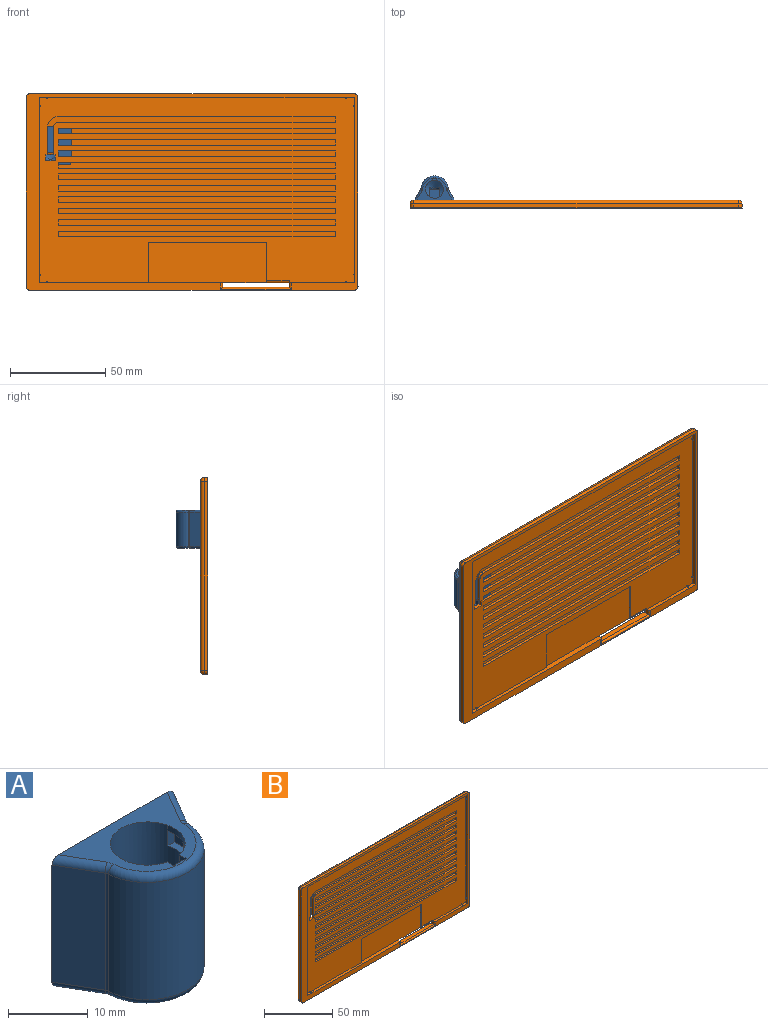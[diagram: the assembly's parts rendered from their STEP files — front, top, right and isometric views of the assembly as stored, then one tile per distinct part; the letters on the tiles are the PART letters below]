
ASSEMBLY  parts=2 mates=1
PART A: 43 faces, bbox 23.9x16.6x22.3 mm
  f0: plane 8.9x4.8mm, normal (0,0,1), area 1.2mm2, adj f21,f32,f34,f40
  f1: cylinder r=4.7mm len=15mm, axis (0,0,1), area 384mm2, adj f2,f7,f21,f23,f25,f31,f32,f33
  f2: cylinder r=4.7mm len=5.57mm, axis (0,0,1), area 6.6mm2, adj f1,f7,f24,f27
  f3: plane 18x5.99mm, normal (-0.86,-0.5,0), area 124.6mm2, adj f6,f11,f17,f20
  f4: cylinder r=7.2mm len=18mm, axis (0,0,-1), area 391.8mm2, adj f12,f13,f17,f18
  f5: plane 18x5.99mm, normal (0.86,-0.5,0), area 124.6mm2, adj f6,f9,f13,f14
  f6: plane 21.84x20.24mm, normal (0,1,0), area 406mm2, adj f3,f5,f7,f8,f9,f11,f14,f20
  f7: plane 19.29x12.2mm, normal (0,0,1), area 83.6mm2, adj f1,f2,f6,f9,f10,f11,f12,f15
  f8: plane 19.29x12.2mm, normal (0,0,-1), area 155.3mm2, adj f6,f14,f16,f18,f19,f20
  f9: cylinder r=1mm len=6.49mm, axis (-0.5,-0.86,0), area 10.4mm2, adj f5,f6,f7,f10
  f10: torus R=2mm, axis (0,0,1), area 1mm2, adj f7,f9,f12,f13
  f11: cylinder r=1mm len=6.49mm, axis (-0.5,0.86,0), area 10.4mm2, adj f3,f6,f7,f15
  f12: torus R=6.2mm, axis (0,0,1), area 32.5mm2, adj f4,f7,f10,f15
  f13: cylinder r=1mm len=18mm, axis (0,0,-1), area 8.4mm2, adj f4,f5,f10,f16
  f14: cylinder r=1mm len=6.49mm, axis (0.5,0.86,0), area 10.4mm2, adj f5,f6,f8,f16
  f15: torus R=2mm, axis (0,0,1), area 1mm2, adj f7,f11,f12,f17
  f16: torus R=2mm, axis (0,0,1), area 1mm2, adj f8,f13,f14,f18
  f17: cylinder r=1mm len=18mm, axis (0,0,-1), area 8.4mm2, adj f3,f4,f15,f19
  f18: torus R=6.2mm, axis (0,0,1), area 32.5mm2, adj f4,f8,f16,f19
  f19: torus R=2mm, axis (0,0,1), area 1mm2, adj f8,f17,f18,f20
  f20: cylinder r=1mm len=6.49mm, axis (0.5,-0.86,0), area 10.4mm2, adj f3,f6,f8,f19
  f21: cone r=0mm half-angle=57.4deg, axis (0,0,1), area 41.7mm2, adj f0,f1,f39,f40,f41
  f22: plane 3.1x2.2mm, normal (0,1,0), area 6.8mm2, adj f7,f23,f24,f25,f28
  f23: plane 6.8x6.7mm, normal (0,0,1), area 9.2mm2, adj f1,f22,f25,f26,f28,f29,f30,f31
  f24: plane 1.13x0.9mm, normal (-1,0,0), area 1mm2, adj f2,f7,f22,f27
  f25: plane 3.1x1.13mm, normal (1,0,0), area 3.5mm2, adj f1,f7,f22,f23
  f26: cylinder r=5.5mm len=4.04mm, axis (0,0,-1), area 11.8mm2, adj f23,f27,f28,f30
  f27: plane 6.7x4.6mm, normal (0,0,-1), area 6.9mm2, adj f2,f24,f26,f28,f29,f30,f31
  f28: cylinder r=5mm len=2.2mm, axis (0,0,1), area 2.8mm2, adj f22,f23,f26,f27
  f29: plane 2.2x2mm, normal (-1,0,0), area 4.4mm2, adj f23,f27,f30,f31
  f30: plane 2.2x0.29mm, normal (0,1,0), area 0.6mm2, adj f23,f26,f27,f29
  f31: plane 2.2x1.11mm, normal (0,-1,0), area 2.4mm2, adj f1,f23,f27,f29
  f32: plane 2x0.1mm, normal (-1,0,0), area 0.2mm2, adj f0,f1,f33,f34
  f33: plane 9.6x4.8mm, normal (0,0,-1), area 1.5mm2, adj f1,f32,f34,f35
  f34: cylinder r=4.8mm len=9.6mm, axis (0,0,-1), area 30.2mm2, adj f0,f32,f33,f35,f37
  f35: plane 2x0.1mm, normal (-1,0,0), area 0.2mm2, adj f1,f33,f34,f37
  f36: plane 6.2x5mm, normal (0,0,1), area 31mm2, adj f6,f38,f39,f40
  f37: plane 5x1.22mm, normal (0,0,-1), area 3.4mm2, adj f1,f34,f35,f39,f40,f42
  f38: plane 5x1.53mm, normal (0,1,0), area 4.4mm2, adj f36,f39,f40,f41
  f39: plane 9.29x7.26mm, normal (-1,0,0), area 21.7mm2, adj f6,f21,f36,f37,f38,f41,f42
  f40: plane 9.29x7.26mm, normal (1,0,0), area 21.7mm2, adj f0,f6,f21,f36,f37,f38,f41,f42
  f41: bspline ~7.09x2.62mm, area 6.9mm2, adj f21,f38,f39,f40
  f42: cylinder r=1mm len=5mm, axis (-1,0,0), area 7.9mm2, adj f6,f37,f39,f40
PART B: 133 faces, bbox 174x4x103 mm
  f0: plane 2x0.94mm, normal (0,0,-1), area 1.9mm2, adj f2,f38,f40,f57
  f1: plane 62x21mm, normal (0,-1,0), area 1302mm2, adj f3,f4,f5,f102,f127
  f2: plane 170x99mm, normal (0,1,0), area 16703.9mm2, adj f0,f38,f39,f40,f41,f42,f43,f119
  f3: plane 21x1mm, normal (-1,0,0), area 20.8mm2, adj f1,f4,f57,f127
  f4: plane 62x1mm, normal (0,0,-1), area 62mm2, adj f1,f3,f5,f57
  f5: plane 21x1mm, normal (1,0,0), area 21mm2, adj f1,f4,f57,f102
  f6: plane 3x1.5mm, normal (1,0,0), area 4.5mm2, adj f7,f56,f57,f59
  f7: plane 145x1.5mm, normal (0,0,-1), area 217.5mm2, adj f6,f8,f57,f59
  f8: plane 3x1.5mm, normal (-1,0,0), area 4.5mm2, adj f7,f56,f57,f59
  f9: plane 3x1.5mm, normal (1,0,0), area 4.5mm2, adj f10,f46,f57,f60
  f10: plane 145x1.5mm, normal (0,0,-1), area 217.5mm2, adj f9,f11,f57,f60
  f11: plane 3x1.5mm, normal (-1,0,0), area 4.5mm2, adj f10,f46,f57,f60
  f12: plane 3x1.5mm, normal (1,0,0), area 4.5mm2, adj f13,f47,f57,f61
  f13: plane 145x1.5mm, normal (0,0,-1), area 217.5mm2, adj f12,f14,f57,f61
  f14: plane 3x1.5mm, normal (-1,0,0), area 4.5mm2, adj f13,f47,f57,f61
  f15: plane 3x1.5mm, normal (1,0,0), area 4.5mm2, adj f16,f48,f57,f62
  f16: plane 145x1.5mm, normal (0,0,-1), area 217.5mm2, adj f15,f17,f57,f62
  f17: plane 3x1.5mm, normal (-1,0,0), area 4.5mm2, adj f16,f48,f57,f62
  f18: plane 3x1.5mm, normal (1,0,0), area 4.5mm2, adj f19,f49,f57,f63
  f19: plane 145x1.5mm, normal (0,0,-1), area 217.5mm2, adj f18,f20,f57,f63
  f20: plane 3x1.5mm, normal (-1,0,0), area 4.5mm2, adj f19,f49,f57,f63
  f21: plane 3x1.5mm, normal (1,0,0), area 4.5mm2, adj f22,f50,f57,f64
  f22: plane 145x1.5mm, normal (0,0,-1), area 217.5mm2, adj f21,f23,f57,f64
  f23: plane 3x1.5mm, normal (-1,0,0), area 4.5mm2, adj f22,f50,f57,f64
  f24: plane 3x1.5mm, normal (1,0,0), area 4.5mm2, adj f25,f51,f57,f65
  f25: plane 145x1.5mm, normal (0,0,-1), area 217.5mm2, adj f24,f26,f57,f65
  f26: plane 3x1.5mm, normal (-1,0,0), area 4.5mm2, adj f25,f51,f57,f65
  f27: plane 3x1.5mm, normal (1,0,0), area 4.5mm2, adj f28,f52,f57,f66
  f28: plane 145x1.5mm, normal (0,0,-1), area 217.5mm2, adj f27,f29,f57,f66
  f29: plane 3x1.5mm, normal (-1,0,0), area 4.5mm2, adj f28,f52,f57,f66
  f30: plane 3x1.5mm, normal (1,0,0), area 4.5mm2, adj f31,f53,f57,f67
  f31: plane 145x1.5mm, normal (0,0,-1), area 217.5mm2, adj f30,f32,f57,f67
  f32: plane 3x1.5mm, normal (-1,0,0), area 4.5mm2, adj f31,f53,f57,f67
  f33: plane 3x1.5mm, normal (1,0,0), area 4.5mm2, adj f34,f54,f57,f68
  f34: plane 145x1.5mm, normal (0,0,-1), area 217.5mm2, adj f33,f35,f57,f68
  f35: plane 3x1.5mm, normal (-1,0,0), area 4.5mm2, adj f34,f54,f57,f68
  f36: plane 145x1.5mm, normal (0,0,1), area 217.5mm2, adj f37,f55,f57,f58
  f37: cylinder r=2.64mm len=2.64mm, axis (0,1,0), area 6.2mm2, adj f36,f38,f57,f58
  f38: plane 14.36x2mm, normal (-1,0,0), area 21.7mm2, adj f0,f2,f37,f57,f58,f132
  f39: plane 2x0.96mm, normal (0,0,-1), area 1.9mm2, adj f2,f42,f43,f57
  f40: plane 3x2mm, normal (-1,0,0), area 6mm2, adj f0,f2,f41,f57
  f41: plane 4.9x2mm, normal (0,0,1), area 9.8mm2, adj f2,f40,f42,f57
  f42: plane 3x2mm, normal (1,0,0), area 6mm2, adj f2,f39,f41,f57
  f43: plane 14.36x2mm, normal (1,0,0), area 21.7mm2, adj f2,f39,f44,f57,f58,f132
  f44: cylinder r=5.64mm len=5.64mm, axis (0,1,0), area 13.3mm2, adj f43,f45,f57,f58
  f45: plane 145x1.5mm, normal (0,0,-1), area 217.5mm2, adj f44,f55,f57,f58
  f46: plane 145x1.5mm, normal (0,0,1), area 217.5mm2, adj f9,f11,f57,f60
  f47: plane 145x1.5mm, normal (0,0,1), area 217.5mm2, adj f12,f14,f57,f61
  f48: plane 145x1.5mm, normal (0,0,1), area 217.5mm2, adj f15,f17,f57,f62
  f49: plane 145x1.5mm, normal (0,0,1), area 217.5mm2, adj f18,f20,f57,f63
  f50: plane 145x1.5mm, normal (0,0,1), area 217.5mm2, adj f21,f23,f57,f64
  f51: plane 145x1.5mm, normal (0,0,1), area 217.5mm2, adj f24,f26,f57,f65
  f52: plane 145x1.5mm, normal (0,0,1), area 217.5mm2, adj f27,f29,f57,f66
  f53: plane 145x1.5mm, normal (0,0,1), area 217.5mm2, adj f30,f32,f57,f67
  f54: plane 145x1.5mm, normal (0,0,1), area 217.5mm2, adj f33,f35,f57,f68
  f55: plane 3x1.5mm, normal (-1,0,0), area 4.5mm2, adj f36,f45,f57,f58
  f56: plane 145x1.5mm, normal (0,0,1), area 217.5mm2, adj f6,f8,f57,f59
  f57: plane 165x97mm, normal (0,-1,0), area 9826.7mm2, adj f0,f3,f4,f5,f6,f7,f8,f9
  f58: plane 150.64x19mm, normal (0,-1,0), area 494.6mm2, adj f36,f37,f38,f43,f44,f45,f55,f132
  f59: plane 145x3mm, normal (0,-1,0), area 435mm2, adj f6,f7,f8,f56
  f60: plane 145x3mm, normal (0,-1,0), area 435mm2, adj f9,f10,f11,f46
  f61: plane 145x3mm, normal (0,-1,0), area 435mm2, adj f12,f13,f14,f47
  f62: plane 145x3mm, normal (0,-1,0), area 435mm2, adj f15,f16,f17,f48
  f63: plane 145x3mm, normal (0,-1,0), area 435mm2, adj f18,f19,f20,f49
  f64: plane 145x3mm, normal (0,-1,0), area 435mm2, adj f21,f22,f23,f50
  f65: plane 145x3mm, normal (0,-1,0), area 435mm2, adj f24,f25,f26,f51
  f66: plane 145x3mm, normal (0,-1,0), area 435mm2, adj f27,f28,f29,f52
  f67: plane 145x3mm, normal (0,-1,0), area 435mm2, adj f30,f31,f32,f53
  f68: plane 145x3mm, normal (0,-1,0), area 435mm2, adj f33,f34,f35,f54
  f69: plane 1x0.5mm, normal (1,0,0), area 0.5mm2, adj f57,f70,f72,f101
  f70: plane 1x0.5mm, normal (0,0,-1), area 0.5mm2, adj f57,f69,f71,f72
  f71: plane 1x0.5mm, normal (-1,0,0), area 0.5mm2, adj f57,f70,f72,f101
  f72: plane 0.5x0.5mm, normal (0,-1,0), area 0.3mm2, adj f69,f70,f71,f101
  f73: plane 1x0.5mm, normal (1,0,0), area 0.5mm2, adj f57,f74,f76,f101
  f74: plane 1x0.5mm, normal (0,0,-1), area 0.5mm2, adj f57,f73,f75,f76
  f75: plane 1x0.5mm, normal (-1,0,0), area 0.5mm2, adj f57,f74,f76,f101
  f76: plane 0.5x0.5mm, normal (0,-1,0), area 0.3mm2, adj f73,f74,f75,f101
  f77: plane 1x0.5mm, normal (-1,0,0), area 0.5mm2, adj f57,f78,f80,f102
  f78: plane 1x0.5mm, normal (0,0,1), area 0.5mm2, adj f57,f77,f79,f80
  f79: plane 1x0.5mm, normal (1,0,0), area 0.5mm2, adj f57,f78,f80,f102
  f80: plane 0.5x0.5mm, normal (0,-1,0), area 0.3mm2, adj f77,f78,f79,f102
  f81: plane 1x0.5mm, normal (0,0,1), area 0.5mm2, adj f57,f82,f84,f103
  f82: plane 1x0.5mm, normal (1,0,0), area 0.5mm2, adj f57,f81,f83,f84
  f83: plane 1x0.5mm, normal (0,0,-1), area 0.5mm2, adj f57,f82,f84,f103
  f84: plane 0.5x0.5mm, normal (0,-1,0), area 0.3mm2, adj f81,f82,f83,f103
  f85: plane 1x0.5mm, normal (1,0,0), area 0.5mm2, adj f57,f86,f87,f88
  f86: plane 1x0.5mm, normal (0,0,-1), area 0.5mm2, adj f57,f85,f88,f103
  f87: plane 1x0.5mm, normal (0,0,1), area 0.5mm2, adj f57,f85,f88,f103
  f88: plane 0.5x0.5mm, normal (0,-1,0), area 0.3mm2, adj f85,f86,f87,f103
  f89: plane 1x0.5mm, normal (0,0,-1), area 0.5mm2, adj f57,f90,f92,f104
  f90: plane 1x0.5mm, normal (-1,0,0), area 0.5mm2, adj f57,f89,f91,f92
  f91: plane 1x0.5mm, normal (0,0,1), area 0.5mm2, adj f57,f90,f92,f104
  f92: plane 0.5x0.5mm, normal (0,-1,0), area 0.3mm2, adj f89,f90,f91,f104
  f93: plane 1x0.5mm, normal (0,0,-1), area 0.5mm2, adj f57,f94,f96,f104
  f94: plane 1x0.5mm, normal (-1,0,0), area 0.5mm2, adj f57,f93,f95,f96
  f95: plane 1x0.5mm, normal (0,0,1), area 0.5mm2, adj f57,f94,f96,f104
  f96: plane 0.5x0.5mm, normal (0,-1,0), area 0.3mm2, adj f93,f94,f95,f104
  f97: plane 1x0.5mm, normal (0,0,1), area 0.5mm2, adj f57,f98,f99,f100
  f98: plane 1x0.5mm, normal (1,0,0), area 0.5mm2, adj f57,f97,f100,f105
  f99: plane 1x0.5mm, normal (-1,0,0), area 0.5mm2, adj f57,f97,f100,f105
  f100: plane 0.5x0.5mm, normal (0,-1,0), area 0.3mm2, adj f97,f98,f99,f105
  f101: plane 165x2mm, normal (0,0,-1), area 329mm2, adj f57,f69,f71,f72,f73,f75,f76,f103
  f102: plane 96x3mm, normal (0,0,1), area 230.3mm2, adj f1,f5,f57,f77,f79,f80,f103,f108
  f103: plane 97x2mm, normal (1,0,0), area 193mm2, adj f57,f81,f83,f84,f86,f87,f88,f101
  f104: plane 97x2mm, normal (-1,0,0), area 193mm2, adj f57,f89,f91,f92,f93,f95,f96,f101
  f105: plane 34x2mm, normal (0,0,1), area 67.3mm2, adj f57,f98,f99,f100,f104,f106,f117,f129
  f106: plane 3.5x2mm, normal (-1,0,0), area 5.2mm2, adj f57,f105,f107,f127,f128,f129
  f107: plane 36.3x2.94mm, normal (0,0,1), area 103.1mm2, adj f106,f108,f123,f126,f128,f130
  f108: plane 2.5x2mm, normal (1,0,0), area 5mm2, adj f102,f107,f126,f131
  f109: cylinder r=2mm len=2mm, axis (0,1,0), area 6.3mm2, adj f110,f116,f117,f122
  f110: plane 170x2mm, normal (0,0,1), area 340mm2, adj f109,f111,f117,f120
  f111: cylinder r=2mm len=2mm, axis (0,1,0), area 6.3mm2, adj f110,f112,f117,f118
  f112: plane 99x2mm, normal (-1,0,0), area 198mm2, adj f111,f113,f117,f119
  f113: cylinder r=2mm len=2mm, axis (0,1,0), area 6.3mm2, adj f112,f114,f117,f121
  f114: plane 170x2mm, normal (0,0,-1), area 340mm2, adj f113,f115,f117,f123
  f115: cylinder r=2mm len=2mm, axis (0,1,0), area 6.3mm2, adj f114,f116,f117,f125
  f116: plane 99x2mm, normal (1,0,0), area 198mm2, adj f109,f115,f117,f124
  f117: plane 174x103mm, normal (0,-1,0), area 1784.1mm2, adj f101,f102,f103,f104,f105,f109,f110,f111
  f118: sphere r=2mm, area 6.3mm2, adj f111,f119,f120
  f119: cylinder r=2mm len=99mm, axis (0,0,-1), area 311mm2, adj f2,f112,f118,f121
  f120: cylinder r=2mm len=170mm, axis (-1,0,0), area 534.1mm2, adj f2,f110,f118,f122
  f121: sphere r=2mm, area 6.3mm2, adj f113,f119,f123
  f122: sphere r=2mm, area 6.3mm2, adj f109,f120,f124
  f123: cylinder r=2mm len=170mm, axis (1,0,0), area 515.5mm2, adj f2,f107,f114,f121,f125,f126,f128
  f124: cylinder r=2mm len=99mm, axis (0,0,1), area 311mm2, adj f2,f116,f122,f125
  f125: sphere r=2mm, area 6.3mm2, adj f115,f123,f124
  f126: cylinder r=1mm len=3.5mm, axis (0,0,1), area 4.4mm2, adj f2,f107,f108,f123,f127
  f127: cylinder r=1mm len=37mm, axis (-1,0,0), area 75mm2, adj f1,f2,f3,f57,f106,f126,f128
  f128: cylinder r=1mm len=3.5mm, axis (0,0,-1), area 4.4mm2, adj f2,f106,f107,f123,f127
  f129: cylinder r=1mm len=3.5mm, axis (0,0,1), area 4.5mm2, adj f105,f106,f117,f130
  f130: cylinder r=1mm len=37mm, axis (1,0,0), area 56.1mm2, adj f107,f117,f129,f131
  f131: cylinder r=1mm len=3.5mm, axis (0,0,-1), area 4.5mm2, adj f102,f108,f117,f130
  f132: cylinder r=1mm len=3mm, axis (-1,0,0), area 3.1mm2, adj f2,f38,f43,f58
PLACE A rot(axis=(0,0,1),180deg) t=(-77.9,-32.27,24)mm
PLACE B rot(axis=(0,-1,0),0deg) t=(-1.27,-37.97,5.5)mm
MATE slider B.f58 <-> A.f6  axis (0,1,0) through (-77.9,-38.47,25)mm
